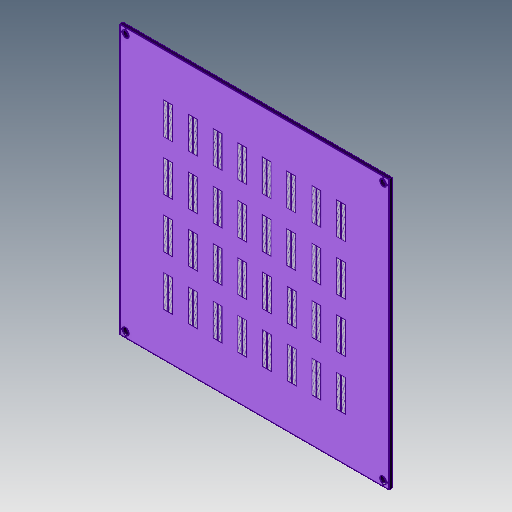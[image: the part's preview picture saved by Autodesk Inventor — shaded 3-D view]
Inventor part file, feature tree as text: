
AUTODESK INVENTOR PART (.ipt)
format: ipt  version: 2017 (Build 210142000, 142)  size: 233,984 bytes
history: native  units: mm
features: other x4, sketch x2
ambient origin geometry x8: Origin, YZ Plane, XZ Plane, XY Plane, X Axis, Y Axis, Z Axis, Center Point
bodies: Solid1 (feature_tree)
feature tree (6):
  other  "Decal1"
  other  "Decal2"
  sketch  "Sketch1"
  other  "Image1"
  sketch  "Sketch2"
  other  "Image2"
